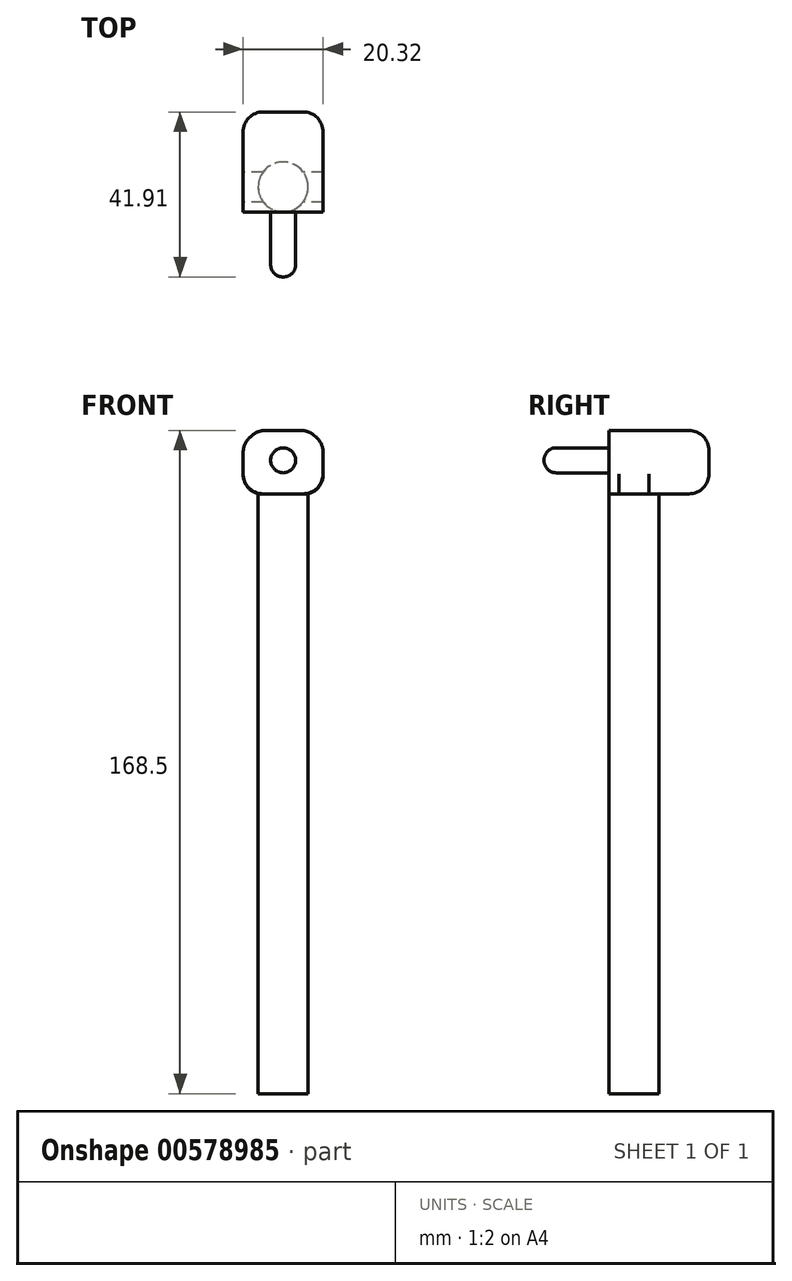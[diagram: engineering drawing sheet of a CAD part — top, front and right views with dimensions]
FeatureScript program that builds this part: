
annotation { "Feature Type Name" : "Feature", "Feature Type Description" : "" }
export const myFeature = defineFeature(function(context is Context, id is Id, definition is map)
    precondition{}
    {
        {
            var Q0;
            Q0=qCreatedBy(makeId("Front.planeOp"),FACE);
            var sketch = newSketch(context, id + "F0", { "sketchPlane" : qUnion([Q0])});
            skLineSegment(sketch, "E0", {"start": v(-54.93, -46.36) * mm, "end": v(-54.93, 106.04) * mm});
            skLineSegment(sketch, "E1", {"start": v(-54.93, 106.04) * mm, "end": v(-61.28, 106.04) * mm});
            skLineSegment(sketch, "E2", {"start": v(-54.93, -46.36) * mm, "end": v(-61.28, -46.36) * mm});
            skLineSegment(sketch, "E3", {"start": v(-61.28, -46.36) * mm, "end": v(-61.28, 106.04) * mm});
            skLineSegment(sketch, "E4", {"start": v(-61.28, 106.04) * mm, "end": v(-65.1, 106.04) * mm});
            skLineSegment(sketch, "E5", {"start": v(-65.1, 106.04) * mm, "end": v(-65.1, 118.94) * mm});
            skLineSegment(sketch, "E6", {"start": v(-65.1, 118.94) * mm, "end": v(-61.28, 122.14) * mm});
            skLineSegment(sketch, "E7", {"start": v(-61.28, 122.14) * mm, "end": v(-48.58, 122.14) * mm});
            skLineSegment(sketch, "E8", {"start": v(-48.58, 122.14) * mm, "end": v(-44.77, 118.94) * mm});
            skLineSegment(sketch, "E9", {"start": v(-44.77, 118.94) * mm, "end": v(-44.77, 106.04) * mm});
            skLineSegment(sketch, "E10", {"start": v(-44.77, 106.04) * mm, "end": v(-54.93, 106.04) * mm});
            skSolve(sketch);
        }
        {
            var Q0;
            Q0=makeQuery(id+"F0.imprint","IMPRINT",FACE,{"disambiguationData":[TD([[makeQuery(id+"F0.imprint","IMPRINT",EDGE,{"derivedFrom":sQuery(id+"F0.wireOp",EDGE,"E0")}),1.0]])]});
            var Q1;
            Q1=sQuery(id+"F0.wireOp",EDGE,"E0");
            revolve(context, id + "F1", {"entities" : qUnion([Q0]), "axis" : qUnion([Q1]), "revolveType" : RevolveType.FULL});
        }
        {
            var Q0;
            Q0=makeQuery(id+"F0.imprint","IMPRINT",FACE,{"disambiguationData":[TD([[makeQuery(id+"F0.imprint","IMPRINT",EDGE,{"derivedFrom":sQuery(id+"F0.wireOp",EDGE,"E1")}),-1.0]])]});
            extrude(context, id + "F2", {"entities" : qUnion([Q0]), "operationType" : NewBodyOperationType.ADD, "depth" : 6.35 * mm, "offsetDistance" : 25.4 * mm, "hasSecondDirection" : true, "secondDirectionOppositeDirection" : true, "secondDirectionDepth" : 19.05 * mm});
        }
        {
            var Q0;
            Q0=makeQuery(id+"F2.opExtrude","CAP_FACE",FACE,{"disambiguationData":[OSD([sQuery(id+"F0.wireOp",EDGE,"E1"),sQuery(id+"F0.wireOp",EDGE,"E4"),sQuery(id+"F0.wireOp",EDGE,"E5"),sQuery(id+"F0.wireOp",EDGE,"E6"),sQuery(id+"F0.wireOp",EDGE,"E7"),sQuery(id+"F0.wireOp",EDGE,"E8"),sQuery(id+"F0.wireOp",EDGE,"E9"),sQuery(id+"F0.wireOp",EDGE,"E10")])],"isStart":false});
            var sketch = newSketch(context, id + "F3", { "sketchPlane" : qUnion([Q0])});
            skCircle(sketch, "E11", {"center": v(-54.93, 114.55) * mm, "radius": 3.18 * mm});
            skPoint(sketch, "E11.centerSnap0", {"position": v(-54.93, 122.14) * mm});
            skSolve(sketch);
        }
        {
            var Q0;
            Q0=makeQuery(id+"F3.imprint","IMPRINT",FACE,{"disambiguationData":[TD([[makeQuery(id+"F3.imprint","IMPRINT",EDGE,{"derivedFrom":sQuery(id+"F3.wireOp",EDGE,"E11")}),1.0]])]});
            extrude(context, id + "F4", {"entities" : qUnion([Q0]), "operationType" : NewBodyOperationType.ADD, "depth" : 16.5 * mm, "offsetDistance" : 25.4 * mm});
        }
        {
            var Q0;
            Q0=makeQuery(id+"F2.opExtrude","SWEPT_EDGE",EDGE,{"disambiguationData":[OSD([sQuery(id+"F0.wireOp",EDGE,"E8"),sQuery(id+"F0.wireOp",EDGE,"E9")])]});
            var Q1;
            Q1=makeQuery(id+"F2.opExtrude","SWEPT_EDGE",EDGE,{"disambiguationData":[OSD([sQuery(id+"F0.wireOp",EDGE,"E7"),sQuery(id+"F0.wireOp",EDGE,"E8")])]});
            var Q2;
            Q2=makeQuery(id+"F2.opExtrude","SWEPT_EDGE",EDGE,{"disambiguationData":[OSD([sQuery(id+"F0.wireOp",EDGE,"E6"),sQuery(id+"F0.wireOp",EDGE,"E7")])]});
            var Q3;
            Q3=makeQuery(id+"F2.opExtrude","SWEPT_EDGE",EDGE,{"disambiguationData":[OSD([sQuery(id+"F0.wireOp",EDGE,"E5"),sQuery(id+"F0.wireOp",EDGE,"E6")])]});
            var Q4;
            Q4=makeQuery(id+"F2.opExtrude","SWEPT_EDGE",EDGE,{"disambiguationData":[OSD([sQuery(id+"F0.wireOp",EDGE,"E4"),sQuery(id+"F0.wireOp",EDGE,"E5")])]});
            var Q5;
            Q5=makeQuery(id+"F2.opExtrude","SWEPT_EDGE",EDGE,{"disambiguationData":[OSD([sQuery(id+"F0.wireOp",EDGE,"E9"),sQuery(id+"F0.wireOp",EDGE,"E10")])]});
            var Q6;
            Q6=makeQuery(id+"F2.opExtrude","CAP_EDGE",EDGE,{"disambiguationData":[OSD([sQuery(id+"F0.wireOp",EDGE,"E9")])],"isStart":true});
            var Q7;
            Q7=makeQuery(id+"F2.opExtrude","CAP_EDGE",EDGE,{"disambiguationData":[OSD([sQuery(id+"F0.wireOp",EDGE,"E5")])],"isStart":true});
            var Q8;
            Q8=makeQuery(id+"F2.opExtrude","CAP_EDGE",EDGE,{"disambiguationData":[OSD([sQuery(id+"F0.wireOp",EDGE,"E1"),sQuery(id+"F0.wireOp",EDGE,"E4"),sQuery(id+"F0.wireOp",EDGE,"E10")])],"isStart":true});
            var Q9;
            Q9=makeQuery(id+"F2.opExtrude","CAP_EDGE",EDGE,{"disambiguationData":[OSD([sQuery(id+"F0.wireOp",EDGE,"E7")])],"isStart":true});
            var Q10;
            Q10=makeQuery(id+"F2.opExtrude","CAP_EDGE",EDGE,{"disambiguationData":[OSD([sQuery(id+"F0.wireOp",EDGE,"E8")])],"isStart":true});
            var Q11;
            Q11=makeQuery(id+"F2.opExtrude","CAP_EDGE",EDGE,{"disambiguationData":[OSD([sQuery(id+"F0.wireOp",EDGE,"E6")])],"isStart":true});
            fillet(context, id + "F5", {"entities" : qUnion([Q0, Q1, Q2, Q3, Q4, Q5, Q6, Q7, Q8, Q9, Q10, Q11]), "radius" : 5.08 * mm, "tangentPropagation" : true, "allowEdgeOverflow" : false});
        }
        {
            var Q0;
            Q0=makeQuery(id+"F4.opExtrude","CAP_EDGE",EDGE,{"disambiguationData":[OSD([sQuery(id+"F3.wireOp",EDGE,"E11")])],"isStart":false});
            fillet(context, id + "F6", {"entities" : qUnion([Q0]), "radius" : 3.07 * mm, "tangentPropagation" : true, "allowEdgeOverflow" : false});
        }
    });
